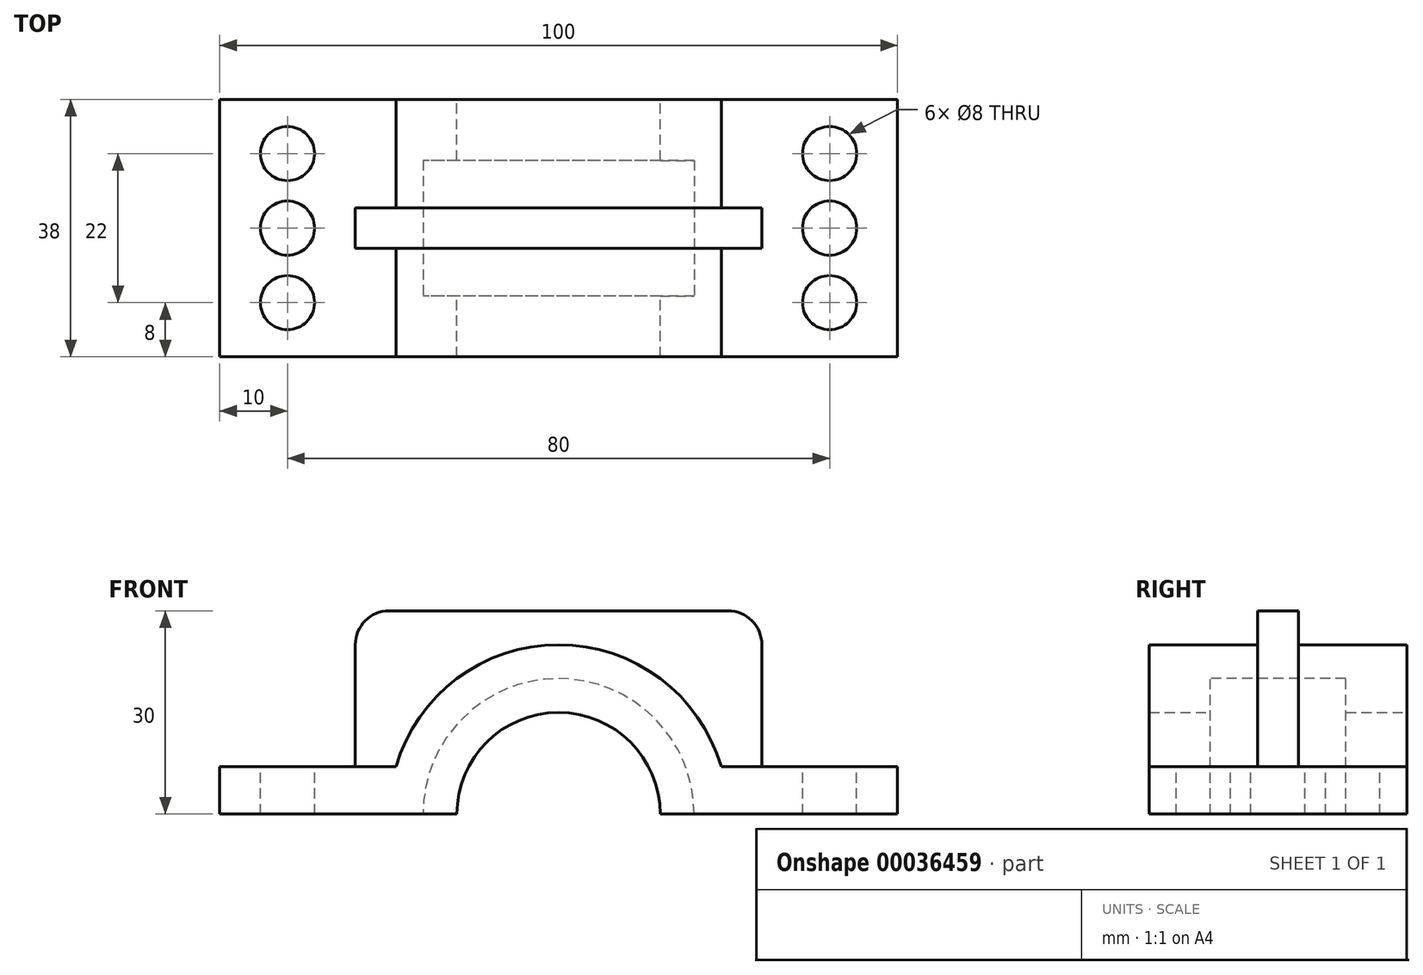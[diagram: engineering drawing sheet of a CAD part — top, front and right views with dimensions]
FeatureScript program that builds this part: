
annotation { "Feature Type Name" : "Feature", "Feature Type Description" : "" }
export const myFeature = defineFeature(function(context is Context, id is Id, definition is map)
    precondition{}
    {
        {
            var Q0;
            Q0=qCreatedBy(makeId("Front.planeOp"),FACE);
            var sketch = newSketch(context, id + "F0", { "sketchPlane" : qUnion([Q0])});
            skArc(sketch, "E0", {"start": v(15, 0) * mm, "mid": v(0, 15) * mm, "end": v(-15, 0) * mm});
            skArc(sketch, "E1", {"start": v(24, 7) * mm, "mid": v(0, 25) * mm, "end": v(-24, 7) * mm});
            skLineSegment(sketch, "E2", {"start": v(-15, 0) * mm, "end": v(-50, 0) * mm});
            skLineSegment(sketch, "E3", {"start": v(-50, 0) * mm, "end": v(-50, 7) * mm});
            skLineSegment(sketch, "E4", {"start": v(-50, 7) * mm, "end": v(-24, 7) * mm});
            skLineSegment(sketch, "E5", {"start": v(15, 0) * mm, "end": v(50, 0) * mm});
            skLineSegment(sketch, "E6", {"start": v(50, 0) * mm, "end": v(50, 7) * mm});
            skLineSegment(sketch, "E7", {"start": v(50, 7) * mm, "end": v(24, 7) * mm});
            skSolve(sketch);
        }
        {
            var Q0;
            Q0=makeQuery(id+"F0.imprint","IMPRINT",FACE,{"disambiguationData":[TD([[makeQuery(id+"F0.imprint","IMPRINT",EDGE,{"derivedFrom":sQuery(id+"F0.wireOp",EDGE,"E0")}),-1.0]])]});
            extrude(context, id + "F1", {"entities" : qUnion([Q0]), "endBound" : BoundingType.SYMMETRIC, "depth" : 38 * mm});
        }
        {
            var Q0;
            Q0=qCreatedBy(makeId("Front.planeOp"),FACE);
            var sketch = newSketch(context, id + "F2", { "sketchPlane" : qUnion([Q0])});
            skCircle(sketch, "E8", {"center": v(0, 0) * mm, "radius": 20 * mm});
            skSolve(sketch);
        }
        {
            var Q0;
            Q0 = qSketchRegion(id + "F2", true);
            extrude(context, id + "F3", {"entities" : qUnion([Q0]), "operationType" : NewBodyOperationType.REMOVE, "endBound" : BoundingType.SYMMETRIC, "oppositeDirection" : true, "depth" : 20 * mm});
        }
        {
            var Q0;
            Q0=qCreatedBy(makeId("Front.planeOp"),FACE);
            var sketch = newSketch(context, id + "F4", { "sketchPlane" : qUnion([Q0])});
            skLineSegment(sketch, "E9", {"start": v(-30, 7) * mm, "end": v(-30, 25) * mm});
            skLineSegment(sketch, "E10", {"start": v(-25, 30) * mm, "end": v(25, 30) * mm});
            skLineSegment(sketch, "E11", {"start": v(30, 25) * mm, "end": v(30, 7) * mm});
            skPoint(sketch, "E12.orphan", {"position": v(-50, 7) * mm});
            skPoint(sketch, "E13.orphan", {"position": v(50, 7) * mm});
            skArc(sketch, "E14.0", {"start": v(24, 7) * mm, "mid": v(0, 25) * mm, "end": v(-24, 7) * mm});
            skLineSegment(sketch, "E15.0", {"start": v(-30, 7) * mm, "end": v(-24, 7) * mm});
            skLineSegment(sketch, "E16.0", {"start": v(30, 7) * mm, "end": v(24, 7) * mm});
            skPoint(sketch, "E17.visualSharp", {"position": v(-30, 30) * mm});
            skArc(sketch, "E17.filletArc", {"start": v(-25, 30) * mm, "mid": v(-28.54, 28.54) * mm, "end": v(-30, 25) * mm});
            skPoint(sketch, "E18.visualSharp", {"position": v(30, 30) * mm});
            skArc(sketch, "E18.filletArc", {"start": v(30, 25) * mm, "mid": v(28.54, 28.54) * mm, "end": v(25, 30) * mm});
            skSolve(sketch);
        }
        {
            var Q0;
            Q0=makeQuery(id+"F4.imprint","IMPRINT",FACE,{"disambiguationData":[TD([[makeQuery(id+"F4.imprint","IMPRINT",EDGE,{"derivedFrom":sQuery(id+"F4.wireOp",EDGE,"E9")}),-1.0]])]});
            extrude(context, id + "F5", {"entities" : qUnion([Q0]), "operationType" : NewBodyOperationType.ADD, "endBound" : BoundingType.SYMMETRIC, "depth" : 6 * mm});
        }
        {
            var Q0;
            Q0=makeQuery(id+"F1.opExtrude","SWEPT_FACE",FACE,{"disambiguationData":[OSD([sQuery(id+"F0.wireOp",EDGE,"E4")])]});
            var sketch = newSketch(context, id + "F6", { "sketchPlane" : qUnion([Q0])});
            skCircle(sketch, "E19", {"center": v(-40, -11) * mm, "radius": 4 * mm});
            skCircle(sketch, "E20.1.0.0", {"center": v(40, -11) * mm, "radius": 4 * mm});
            skLineSegment(sketch, "E20.direction1", {"start": v(-40, -11) * mm, "end": v(40, -11) * mm, "construction": true});
            skCircle(sketch, "E21.1.0.0", {"center": v(-40, 0) * mm, "radius": 4 * mm});
            skCircle(sketch, "E21.1.0.1", {"center": v(40, 0) * mm, "radius": 4 * mm});
            skCircle(sketch, "E21.2.0.0", {"center": v(-40, 11) * mm, "radius": 4 * mm});
            skCircle(sketch, "E21.2.0.1", {"center": v(40, 11) * mm, "radius": 4 * mm});
            skLineSegment(sketch, "E21.direction1", {"start": v(-40, -11) * mm, "end": v(-40, 0) * mm, "construction": true});
            skSolve(sketch);
        }
        {
            var Q0;
            Q0 = qSketchRegion(id + "F6", true);
            extrude(context, id + "F7", {"entities" : qUnion([Q0]), "operationType" : NewBodyOperationType.REMOVE, "endBound" : BoundingType.UP_TO_NEXT, "oppositeDirection" : true, "depth" : 25 * mm});
        }
    });
